# Revit family: Keilhauer-Swav-Low_Back_Conference_Chair-1
name_source: partatom
category: Furniture
units: mm (PartAtom-declared; Revit-internal decimal feet)

## family parameters
Always vertical = Yes
Cut with Voids When Loaded = No
Room Calculation Point = No
Shared = No
Work Plane-Based = No

## types (4) — shared parameters
Assembly Code = E2020200
Default Elevation = 0"
Depth = 22 1/2"
Keynote = 12500
Manufacturer = Keilhauer
Mechanism Finish = <By Category>
Product Documentation Link = https://keilhauer.com
Revit File Built By = https://servex-us.com
Type Comments = Swav
URL = https://keilhauer.com
Width = 23"

## per-type parameters (varying)
| type | Arm | Description |
| 94242 | Yes | Low back conference chair with polished aluminum base |
| 94243 | Yes | Low back conference chair with nylon base |
| 94244 | No | Low back conference armless with aluminum base |
| 94245 | No | Low back conference armless with nylon base |

note: column(s) folded — value = type name in every type: Model

## geometry (parser evidence)
native form markers: Sweep x16
no freeform markers — native parametric forms only
